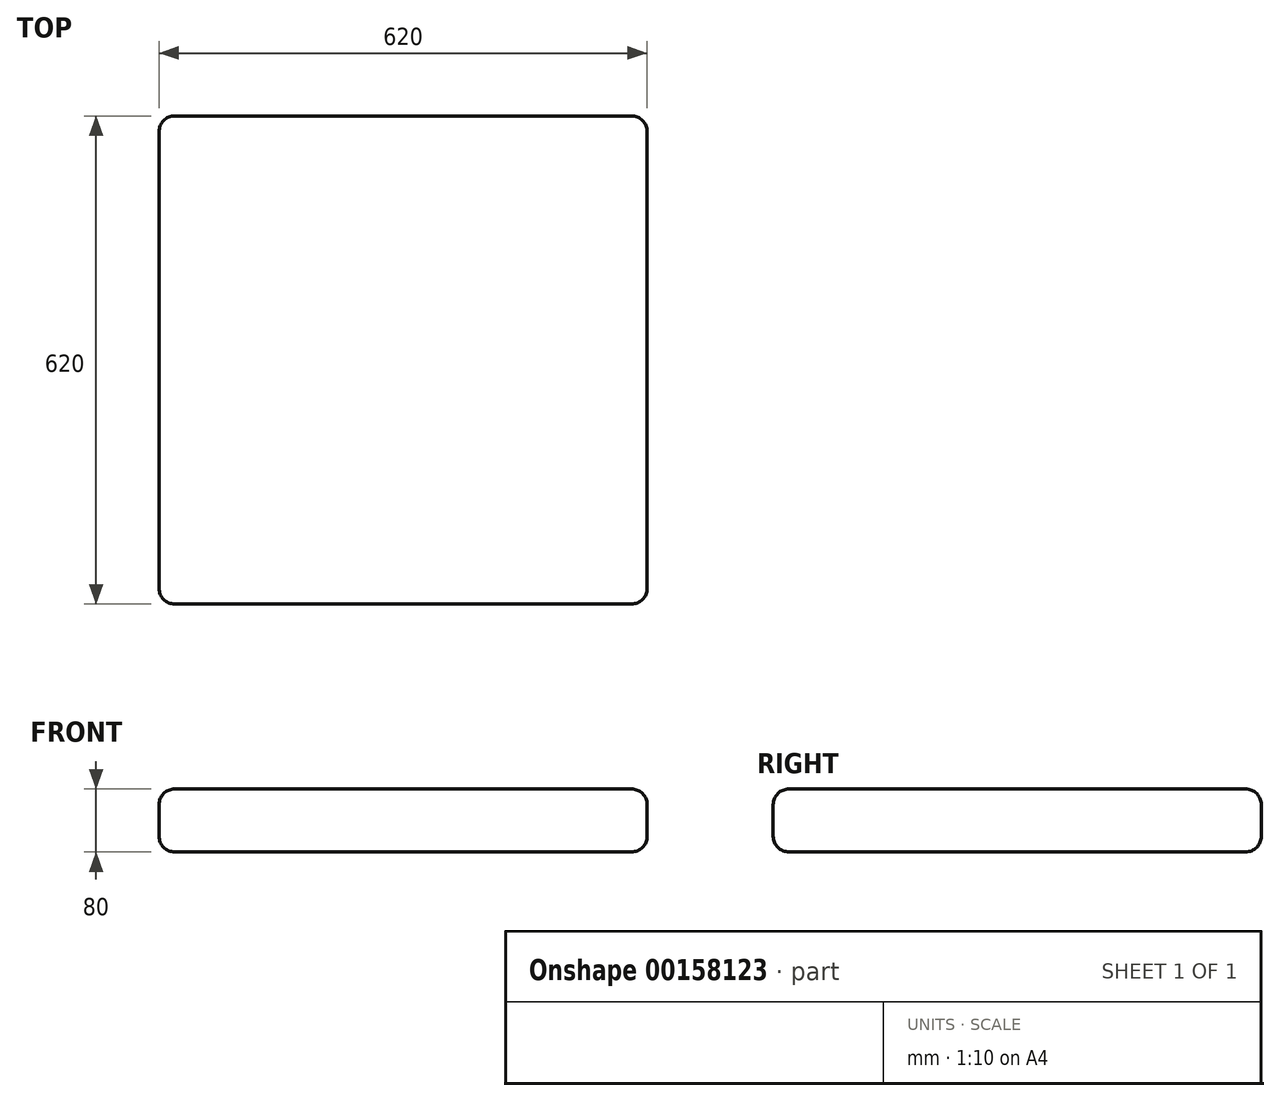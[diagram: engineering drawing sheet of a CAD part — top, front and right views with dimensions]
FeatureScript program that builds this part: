
annotation { "Feature Type Name" : "Feature", "Feature Type Description" : "" }
export const myFeature = defineFeature(function(context is Context, id is Id, definition is map)
    precondition{}
    {
        {
            var Q0;
            Q0=qCreatedBy(makeId("Top.planeOp"),FACE);
            var sketch = newSketch(context, id + "F0", { "sketchPlane" : qUnion([Q0])});
            skLineSegment(sketch, "E0.bottom", {"start": v(310, 310) * mm, "end": v(-310, 310) * mm});
            skLineSegment(sketch, "E0.top", {"start": v(310, -310) * mm, "end": v(-310, -310) * mm});
            skLineSegment(sketch, "E0.left", {"start": v(310, 310) * mm, "end": v(310, -310) * mm});
            skLineSegment(sketch, "E0.right", {"start": v(-310, 310) * mm, "end": v(-310, -310) * mm});
            skPoint(sketch, "E0.middle", {"position": v(0, 0) * mm});
            skSolve(sketch);
        }
        {
            var Q0;
            Q0=makeQuery(id+"F0.imprint","IMPRINT",FACE,{"disambiguationData":[TD([[makeQuery(id+"F0.imprint","IMPRINT",EDGE,{"derivedFrom":sQuery(id+"F0.wireOp",EDGE,"E0.bottom")}),1.0]])]});
            extrude(context, id + "F1", {"entities" : qUnion([Q0]), "endBound" : BoundingType.SYMMETRIC, "depth" : 80 * mm});
        }
        {
            var Q0;
            Q0=makeQuery(id+"F1.opExtrude","CAP_EDGE",EDGE,{"disambiguationData":[OSD([sQuery(id+"F0.wireOp",EDGE,"E0.top")])],"isStart":false});
            var Q1;
            Q1=makeQuery(id+"F1.opExtrude","CAP_EDGE",EDGE,{"disambiguationData":[OSD([sQuery(id+"F0.wireOp",EDGE,"E0.right")])],"isStart":false});
            var Q2;
            Q2=makeQuery(id+"F1.opExtrude","CAP_EDGE",EDGE,{"disambiguationData":[OSD([sQuery(id+"F0.wireOp",EDGE,"E0.bottom")])],"isStart":false});
            var Q3;
            Q3=makeQuery(id+"F1.opExtrude","CAP_EDGE",EDGE,{"disambiguationData":[OSD([sQuery(id+"F0.wireOp",EDGE,"E0.left")])],"isStart":false});
            var Q4;
            Q4=makeQuery(id+"F1.opExtrude","SWEPT_EDGE",EDGE,{"disambiguationData":[OSD([sQuery(id+"F0.wireOp",EDGE,"E0.bottom"),sQuery(id+"F0.wireOp",EDGE,"E0.left")])]});
            var Q5;
            Q5=makeQuery(id+"F1.opExtrude","CAP_EDGE",EDGE,{"disambiguationData":[OSD([sQuery(id+"F0.wireOp",EDGE,"E0.left")])],"isStart":true});
            var Q6;
            Q6=makeQuery(id+"F1.opExtrude","SWEPT_EDGE",EDGE,{"disambiguationData":[OSD([sQuery(id+"F0.wireOp",EDGE,"E0.top"),sQuery(id+"F0.wireOp",EDGE,"E0.left")])]});
            var Q7;
            Q7=makeQuery(id+"F1.opExtrude","CAP_EDGE",EDGE,{"disambiguationData":[OSD([sQuery(id+"F0.wireOp",EDGE,"E0.top")])],"isStart":true});
            var Q8;
            Q8=makeQuery(id+"F1.opExtrude","SWEPT_EDGE",EDGE,{"disambiguationData":[OSD([sQuery(id+"F0.wireOp",EDGE,"E0.top"),sQuery(id+"F0.wireOp",EDGE,"E0.right")])]});
            var Q9;
            Q9=makeQuery(id+"F1.opExtrude","CAP_EDGE",EDGE,{"disambiguationData":[OSD([sQuery(id+"F0.wireOp",EDGE,"E0.right")])],"isStart":true});
            var Q10;
            Q10=makeQuery(id+"F1.opExtrude","SWEPT_EDGE",EDGE,{"disambiguationData":[OSD([sQuery(id+"F0.wireOp",EDGE,"E0.bottom"),sQuery(id+"F0.wireOp",EDGE,"E0.right")])]});
            var Q11;
            Q11=makeQuery(id+"F1.opExtrude","CAP_EDGE",EDGE,{"disambiguationData":[OSD([sQuery(id+"F0.wireOp",EDGE,"E0.bottom")])],"isStart":true});
            fillet(context, id + "F2", {"entities" : qUnion([Q0, Q1, Q2, Q3, Q4, Q5, Q6, Q7, Q8, Q9, Q10, Q11]), "radius" : 20 * mm, "tangentPropagation" : true, "allowEdgeOverflow" : false});
        }
    });
